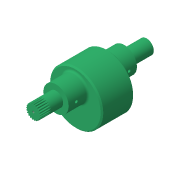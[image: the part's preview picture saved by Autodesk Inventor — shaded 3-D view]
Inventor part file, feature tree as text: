
AUTODESK INVENTOR PART (.ipt)
format: ipt  version: 2016 (Build 200138000, 138)  size: 831,488 bytes
history: native  units: in
note: dims shown in document units (in); Inventor stores cm internally (conversion verified against a paired STEP export)
features: thread x2
ambient origin geometry x8: Origin, YZ Plane, XZ Plane, XY Plane, X Axis, Y Axis, Z Axis, Center Point
bodies: Solid2 (feature_tree), Solid1 (feature_tree)
feature tree (2):
  thread  "Thread1"  [1 undecoded]
  thread  "Thread2"  [1 undecoded]
note: 2 required parameter values undecoded (feature->parameter linkage not recoverable at this tier; creation-order binding heuristic only, values carry confidence <= 0.55)
